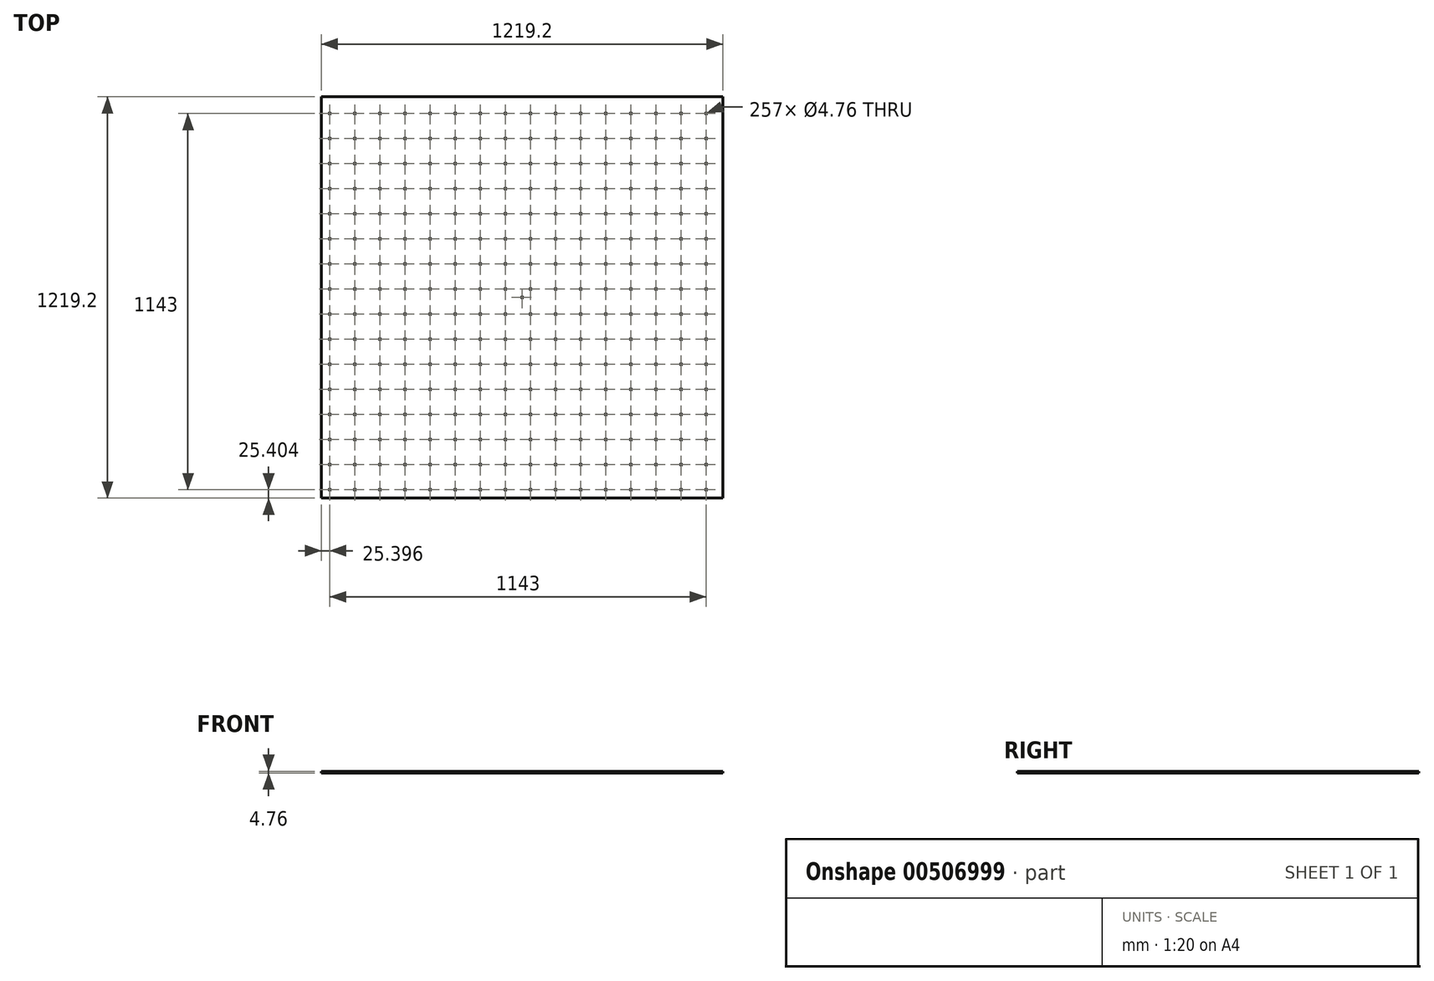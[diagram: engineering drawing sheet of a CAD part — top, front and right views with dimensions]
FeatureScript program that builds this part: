
annotation { "Feature Type Name" : "Feature", "Feature Type Description" : "" }
export const myFeature = defineFeature(function(context is Context, id is Id, definition is map)
    precondition{}
    {
        {
            var Q0;
            Q0=qCreatedBy(makeId("Top.planeOp"),FACE);
            var sketch = newSketch(context, id + "F0", { "sketchPlane" : qUnion([Q0])});
            skLineSegment(sketch, "E0.bottom", {"start": v(-1348, 608.9) * mm, "end": v(-128.8, 608.9) * mm});
            skLineSegment(sketch, "E0.top", {"start": v(-1348, -610.3) * mm, "end": v(-128.8, -610.3) * mm});
            skLineSegment(sketch, "E0.left", {"start": v(-1348, 608.9) * mm, "end": v(-1348, -610.3) * mm});
            skLineSegment(sketch, "E0.right", {"start": v(-128.8, 608.9) * mm, "end": v(-128.8, -610.3) * mm});
            skPoint(sketch, "E0.middle", {"position": v(-738.4, -0.7) * mm});
            skCircle(sketch, "E1", {"center": v(-738.4, -0.7) * mm, "radius": 2.38 * mm});
            skLineSegment(sketch, "E2.bottom", {"start": v(-1348, -610.3) * mm, "end": v(-1322.6, -610.3) * mm, "construction": true});
            skLineSegment(sketch, "E2.top", {"start": v(-1348, -584.9) * mm, "end": v(-1322.6, -584.9) * mm, "construction": true});
            skLineSegment(sketch, "E2.left", {"start": v(-1348, -610.3) * mm, "end": v(-1348, -584.9) * mm, "construction": true});
            skLineSegment(sketch, "E2.right", {"start": v(-1322.6, -610.3) * mm, "end": v(-1322.6, -584.9) * mm, "construction": true});
            skCircle(sketch, "E3", {"center": v(-1322.6, -584.9) * mm, "radius": 2.38 * mm});
            skCircle(sketch, "E4.0.1.0", {"center": v(-1322.6, -508.7) * mm, "radius": 2.38 * mm});
            skCircle(sketch, "E4.0.2.0", {"center": v(-1322.6, -432.5) * mm, "radius": 2.38 * mm});
            skCircle(sketch, "E4.0.3.0", {"center": v(-1322.6, -356.3) * mm, "radius": 2.38 * mm});
            skCircle(sketch, "E4.0.4.0", {"center": v(-1322.6, -280.1) * mm, "radius": 2.38 * mm});
            skCircle(sketch, "E4.0.5.0", {"center": v(-1322.6, -203.9) * mm, "radius": 2.38 * mm});
            skCircle(sketch, "E4.0.6.0", {"center": v(-1322.6, -127.7) * mm, "radius": 2.38 * mm});
            skCircle(sketch, "E4.0.7.0", {"center": v(-1322.6, -51.5) * mm, "radius": 2.38 * mm});
            skCircle(sketch, "E4.0.8.0", {"center": v(-1322.6, 24.7) * mm, "radius": 2.38 * mm});
            skCircle(sketch, "E4.0.9.0", {"center": v(-1322.6, 100.9) * mm, "radius": 2.38 * mm});
            skCircle(sketch, "E4.0.10.0", {"center": v(-1322.6, 177.1) * mm, "radius": 2.38 * mm});
            skCircle(sketch, "E4.1.0.0", {"center": v(-1246.4, -584.9) * mm, "radius": 2.38 * mm});
            skCircle(sketch, "E4.1.1.0", {"center": v(-1246.4, -508.7) * mm, "radius": 2.38 * mm});
            skCircle(sketch, "E4.1.2.0", {"center": v(-1246.4, -432.5) * mm, "radius": 2.38 * mm});
            skCircle(sketch, "E4.1.3.0", {"center": v(-1246.4, -356.3) * mm, "radius": 2.38 * mm});
            skCircle(sketch, "E4.1.4.0", {"center": v(-1246.4, -280.1) * mm, "radius": 2.38 * mm});
            skCircle(sketch, "E4.1.5.0", {"center": v(-1246.4, -203.9) * mm, "radius": 2.38 * mm});
            skCircle(sketch, "E4.1.6.0", {"center": v(-1246.4, -127.7) * mm, "radius": 2.38 * mm});
            skCircle(sketch, "E4.1.7.0", {"center": v(-1246.4, -51.5) * mm, "radius": 2.38 * mm});
            skCircle(sketch, "E4.1.8.0", {"center": v(-1246.4, 24.7) * mm, "radius": 2.38 * mm});
            skCircle(sketch, "E4.1.9.0", {"center": v(-1246.4, 100.9) * mm, "radius": 2.38 * mm});
            skCircle(sketch, "E4.1.10.0", {"center": v(-1246.4, 177.1) * mm, "radius": 2.38 * mm});
            skCircle(sketch, "E4.2.0.0", {"center": v(-1170.2, -584.9) * mm, "radius": 2.38 * mm});
            skCircle(sketch, "E4.2.1.0", {"center": v(-1170.2, -508.7) * mm, "radius": 2.38 * mm});
            skCircle(sketch, "E4.2.2.0", {"center": v(-1170.2, -432.5) * mm, "radius": 2.38 * mm});
            skCircle(sketch, "E4.2.3.0", {"center": v(-1170.2, -356.3) * mm, "radius": 2.38 * mm});
            skCircle(sketch, "E4.2.4.0", {"center": v(-1170.2, -280.1) * mm, "radius": 2.38 * mm});
            skCircle(sketch, "E4.2.5.0", {"center": v(-1170.2, -203.9) * mm, "radius": 2.38 * mm});
            skCircle(sketch, "E4.2.6.0", {"center": v(-1170.2, -127.7) * mm, "radius": 2.38 * mm});
            skCircle(sketch, "E4.2.7.0", {"center": v(-1170.2, -51.5) * mm, "radius": 2.38 * mm});
            skCircle(sketch, "E4.2.8.0", {"center": v(-1170.2, 24.7) * mm, "radius": 2.38 * mm});
            skCircle(sketch, "E4.2.9.0", {"center": v(-1170.2, 100.9) * mm, "radius": 2.38 * mm});
            skCircle(sketch, "E4.2.10.0", {"center": v(-1170.2, 177.1) * mm, "radius": 2.38 * mm});
            skCircle(sketch, "E4.3.0.0", {"center": v(-1094, -584.9) * mm, "radius": 2.38 * mm});
            skCircle(sketch, "E4.3.1.0", {"center": v(-1094, -508.7) * mm, "radius": 2.38 * mm});
            skCircle(sketch, "E4.3.2.0", {"center": v(-1094, -432.5) * mm, "radius": 2.38 * mm});
            skCircle(sketch, "E4.3.3.0", {"center": v(-1094, -356.3) * mm, "radius": 2.38 * mm});
            skCircle(sketch, "E4.3.4.0", {"center": v(-1094, -280.1) * mm, "radius": 2.38 * mm});
            skCircle(sketch, "E4.3.5.0", {"center": v(-1094, -203.9) * mm, "radius": 2.38 * mm});
            skCircle(sketch, "E4.3.6.0", {"center": v(-1094, -127.7) * mm, "radius": 2.38 * mm});
            skCircle(sketch, "E4.3.7.0", {"center": v(-1094, -51.5) * mm, "radius": 2.38 * mm});
            skCircle(sketch, "E4.3.8.0", {"center": v(-1094, 24.7) * mm, "radius": 2.38 * mm});
            skCircle(sketch, "E4.3.9.0", {"center": v(-1094, 100.9) * mm, "radius": 2.38 * mm});
            skCircle(sketch, "E4.3.10.0", {"center": v(-1094, 177.1) * mm, "radius": 2.38 * mm});
            skCircle(sketch, "E4.4.0.0", {"center": v(-1017.8, -584.9) * mm, "radius": 2.38 * mm});
            skCircle(sketch, "E4.4.1.0", {"center": v(-1017.8, -508.7) * mm, "radius": 2.38 * mm});
            skCircle(sketch, "E4.4.2.0", {"center": v(-1017.8, -432.5) * mm, "radius": 2.38 * mm});
            skCircle(sketch, "E4.4.3.0", {"center": v(-1017.8, -356.3) * mm, "radius": 2.38 * mm});
            skCircle(sketch, "E4.4.4.0", {"center": v(-1017.8, -280.1) * mm, "radius": 2.38 * mm});
            skCircle(sketch, "E4.4.5.0", {"center": v(-1017.8, -203.9) * mm, "radius": 2.38 * mm});
            skCircle(sketch, "E4.4.6.0", {"center": v(-1017.8, -127.7) * mm, "radius": 2.38 * mm});
            skCircle(sketch, "E4.4.7.0", {"center": v(-1017.8, -51.5) * mm, "radius": 2.38 * mm});
            skCircle(sketch, "E4.4.8.0", {"center": v(-1017.8, 24.7) * mm, "radius": 2.38 * mm});
            skCircle(sketch, "E4.4.9.0", {"center": v(-1017.8, 100.9) * mm, "radius": 2.38 * mm});
            skCircle(sketch, "E4.4.10.0", {"center": v(-1017.8, 177.1) * mm, "radius": 2.38 * mm});
            skCircle(sketch, "E4.5.0.0", {"center": v(-941.6, -584.9) * mm, "radius": 2.38 * mm});
            skCircle(sketch, "E4.5.1.0", {"center": v(-941.6, -508.7) * mm, "radius": 2.38 * mm});
            skCircle(sketch, "E4.5.2.0", {"center": v(-941.6, -432.5) * mm, "radius": 2.38 * mm});
            skCircle(sketch, "E4.5.3.0", {"center": v(-941.6, -356.3) * mm, "radius": 2.38 * mm});
            skCircle(sketch, "E4.5.4.0", {"center": v(-941.6, -280.1) * mm, "radius": 2.38 * mm});
            skCircle(sketch, "E4.5.5.0", {"center": v(-941.6, -203.9) * mm, "radius": 2.38 * mm});
            skCircle(sketch, "E4.5.6.0", {"center": v(-941.6, -127.7) * mm, "radius": 2.38 * mm});
            skCircle(sketch, "E4.5.7.0", {"center": v(-941.6, -51.5) * mm, "radius": 2.38 * mm});
            skCircle(sketch, "E4.5.8.0", {"center": v(-941.6, 24.7) * mm, "radius": 2.38 * mm});
            skCircle(sketch, "E4.5.9.0", {"center": v(-941.6, 100.9) * mm, "radius": 2.38 * mm});
            skCircle(sketch, "E4.5.10.0", {"center": v(-941.6, 177.1) * mm, "radius": 2.38 * mm});
            skCircle(sketch, "E4.6.0.0", {"center": v(-865.4, -584.9) * mm, "radius": 2.38 * mm});
            skCircle(sketch, "E4.6.1.0", {"center": v(-865.4, -508.7) * mm, "radius": 2.38 * mm});
            skCircle(sketch, "E4.6.2.0", {"center": v(-865.4, -432.5) * mm, "radius": 2.38 * mm});
            skCircle(sketch, "E4.6.3.0", {"center": v(-865.4, -356.3) * mm, "radius": 2.38 * mm});
            skCircle(sketch, "E4.6.4.0", {"center": v(-865.4, -280.1) * mm, "radius": 2.38 * mm});
            skCircle(sketch, "E4.6.5.0", {"center": v(-865.4, -203.9) * mm, "radius": 2.38 * mm});
            skCircle(sketch, "E4.6.6.0", {"center": v(-865.4, -127.7) * mm, "radius": 2.38 * mm});
            skCircle(sketch, "E4.6.7.0", {"center": v(-865.4, -51.5) * mm, "radius": 2.38 * mm});
            skCircle(sketch, "E4.6.8.0", {"center": v(-865.4, 24.7) * mm, "radius": 2.38 * mm});
            skCircle(sketch, "E4.6.9.0", {"center": v(-865.4, 100.9) * mm, "radius": 2.38 * mm});
            skCircle(sketch, "E4.6.10.0", {"center": v(-865.4, 177.1) * mm, "radius": 2.38 * mm});
            skCircle(sketch, "E4.7.0.0", {"center": v(-789.2, -584.9) * mm, "radius": 2.38 * mm});
            skCircle(sketch, "E4.7.1.0", {"center": v(-789.2, -508.7) * mm, "radius": 2.38 * mm});
            skCircle(sketch, "E4.7.2.0", {"center": v(-789.2, -432.5) * mm, "radius": 2.38 * mm});
            skCircle(sketch, "E4.7.3.0", {"center": v(-789.2, -356.3) * mm, "radius": 2.38 * mm});
            skCircle(sketch, "E4.7.4.0", {"center": v(-789.2, -280.1) * mm, "radius": 2.38 * mm});
            skCircle(sketch, "E4.7.5.0", {"center": v(-789.2, -203.9) * mm, "radius": 2.38 * mm});
            skCircle(sketch, "E4.7.6.0", {"center": v(-789.2, -127.7) * mm, "radius": 2.38 * mm});
            skCircle(sketch, "E4.7.7.0", {"center": v(-789.2, -51.5) * mm, "radius": 2.38 * mm});
            skCircle(sketch, "E4.7.8.0", {"center": v(-789.2, 24.7) * mm, "radius": 2.38 * mm});
            skCircle(sketch, "E4.7.9.0", {"center": v(-789.2, 100.9) * mm, "radius": 2.38 * mm});
            skCircle(sketch, "E4.7.10.0", {"center": v(-789.2, 177.1) * mm, "radius": 2.38 * mm});
            skCircle(sketch, "E4.8.0.0", {"center": v(-713, -584.9) * mm, "radius": 2.38 * mm});
            skCircle(sketch, "E4.8.1.0", {"center": v(-713, -508.7) * mm, "radius": 2.38 * mm});
            skCircle(sketch, "E4.8.2.0", {"center": v(-713, -432.5) * mm, "radius": 2.38 * mm});
            skCircle(sketch, "E4.8.3.0", {"center": v(-713, -356.3) * mm, "radius": 2.38 * mm});
            skCircle(sketch, "E4.8.4.0", {"center": v(-713, -280.1) * mm, "radius": 2.38 * mm});
            skCircle(sketch, "E4.8.5.0", {"center": v(-713, -203.9) * mm, "radius": 2.38 * mm});
            skCircle(sketch, "E4.8.6.0", {"center": v(-713, -127.7) * mm, "radius": 2.38 * mm});
            skCircle(sketch, "E4.8.7.0", {"center": v(-713, -51.5) * mm, "radius": 2.38 * mm});
            skCircle(sketch, "E4.8.8.0", {"center": v(-713, 24.7) * mm, "radius": 2.38 * mm});
            skCircle(sketch, "E4.8.9.0", {"center": v(-713, 100.9) * mm, "radius": 2.38 * mm});
            skCircle(sketch, "E4.8.10.0", {"center": v(-713, 177.1) * mm, "radius": 2.38 * mm});
            skCircle(sketch, "E4.9.0.0", {"center": v(-636.8, -584.9) * mm, "radius": 2.38 * mm});
            skCircle(sketch, "E4.9.1.0", {"center": v(-636.8, -508.7) * mm, "radius": 2.38 * mm});
            skCircle(sketch, "E4.9.2.0", {"center": v(-636.8, -432.5) * mm, "radius": 2.38 * mm});
            skCircle(sketch, "E4.9.3.0", {"center": v(-636.8, -356.3) * mm, "radius": 2.38 * mm});
            skCircle(sketch, "E4.9.4.0", {"center": v(-636.8, -280.1) * mm, "radius": 2.38 * mm});
            skCircle(sketch, "E4.9.5.0", {"center": v(-636.8, -203.9) * mm, "radius": 2.38 * mm});
            skCircle(sketch, "E4.9.6.0", {"center": v(-636.8, -127.7) * mm, "radius": 2.38 * mm});
            skCircle(sketch, "E4.9.7.0", {"center": v(-636.8, -51.5) * mm, "radius": 2.38 * mm});
            skCircle(sketch, "E4.9.8.0", {"center": v(-636.8, 24.7) * mm, "radius": 2.38 * mm});
            skCircle(sketch, "E4.9.9.0", {"center": v(-636.8, 100.9) * mm, "radius": 2.38 * mm});
            skCircle(sketch, "E4.9.10.0", {"center": v(-636.8, 177.1) * mm, "radius": 2.38 * mm});
            skCircle(sketch, "E4.10.0.0", {"center": v(-560.6, -584.9) * mm, "radius": 2.38 * mm});
            skCircle(sketch, "E4.10.1.0", {"center": v(-560.6, -508.7) * mm, "radius": 2.38 * mm});
            skCircle(sketch, "E4.10.2.0", {"center": v(-560.6, -432.5) * mm, "radius": 2.38 * mm});
            skCircle(sketch, "E4.10.3.0", {"center": v(-560.6, -356.3) * mm, "radius": 2.38 * mm});
            skCircle(sketch, "E4.10.4.0", {"center": v(-560.6, -280.1) * mm, "radius": 2.38 * mm});
            skCircle(sketch, "E4.10.5.0", {"center": v(-560.6, -203.9) * mm, "radius": 2.38 * mm});
            skCircle(sketch, "E4.10.6.0", {"center": v(-560.6, -127.7) * mm, "radius": 2.38 * mm});
            skCircle(sketch, "E4.10.7.0", {"center": v(-560.6, -51.5) * mm, "radius": 2.38 * mm});
            skCircle(sketch, "E4.10.8.0", {"center": v(-560.6, 24.7) * mm, "radius": 2.38 * mm});
            skCircle(sketch, "E4.10.9.0", {"center": v(-560.6, 100.9) * mm, "radius": 2.38 * mm});
            skCircle(sketch, "E4.10.10.0", {"center": v(-560.6, 177.1) * mm, "radius": 2.38 * mm});
            skCircle(sketch, "E4.11.0.0", {"center": v(-484.4, -584.9) * mm, "radius": 2.38 * mm});
            skCircle(sketch, "E4.11.1.0", {"center": v(-484.4, -508.7) * mm, "radius": 2.38 * mm});
            skCircle(sketch, "E4.11.2.0", {"center": v(-484.4, -432.5) * mm, "radius": 2.38 * mm});
            skCircle(sketch, "E4.11.3.0", {"center": v(-484.4, -356.3) * mm, "radius": 2.38 * mm});
            skCircle(sketch, "E4.11.4.0", {"center": v(-484.4, -280.1) * mm, "radius": 2.38 * mm});
            skCircle(sketch, "E4.11.5.0", {"center": v(-484.4, -203.9) * mm, "radius": 2.38 * mm});
            skCircle(sketch, "E4.11.6.0", {"center": v(-484.4, -127.7) * mm, "radius": 2.38 * mm});
            skCircle(sketch, "E4.11.7.0", {"center": v(-484.4, -51.5) * mm, "radius": 2.38 * mm});
            skCircle(sketch, "E4.11.8.0", {"center": v(-484.4, 24.7) * mm, "radius": 2.38 * mm});
            skCircle(sketch, "E4.11.9.0", {"center": v(-484.4, 100.9) * mm, "radius": 2.38 * mm});
            skCircle(sketch, "E4.11.10.0", {"center": v(-484.4, 177.1) * mm, "radius": 2.38 * mm});
            skLineSegment(sketch, "E4.direction1", {"start": v(-1322.6, -584.9) * mm, "end": v(-1246.4, -584.9) * mm, "construction": true});
            skLineSegment(sketch, "E4.direction2", {"start": v(-1322.6, -584.9) * mm, "end": v(-1322.6, -508.7) * mm, "construction": true});
            skCircle(sketch, "E5.0.12.0", {"center": v(-408.2, -584.9) * mm, "radius": 2.38 * mm});
            skCircle(sketch, "E5.0.12.1", {"center": v(-408.2, -508.7) * mm, "radius": 2.38 * mm});
            skCircle(sketch, "E5.0.12.2", {"center": v(-408.2, -432.5) * mm, "radius": 2.38 * mm});
            skCircle(sketch, "E5.0.12.3", {"center": v(-408.2, -356.3) * mm, "radius": 2.38 * mm});
            skCircle(sketch, "E5.0.12.4", {"center": v(-408.2, -280.1) * mm, "radius": 2.38 * mm});
            skCircle(sketch, "E5.0.12.5", {"center": v(-408.2, -203.9) * mm, "radius": 2.38 * mm});
            skCircle(sketch, "E5.0.12.6", {"center": v(-408.2, -127.7) * mm, "radius": 2.38 * mm});
            skCircle(sketch, "E5.0.12.7", {"center": v(-408.2, -51.5) * mm, "radius": 2.38 * mm});
            skCircle(sketch, "E5.0.12.8", {"center": v(-408.2, 24.7) * mm, "radius": 2.38 * mm});
            skCircle(sketch, "E5.0.12.9", {"center": v(-408.2, 100.9) * mm, "radius": 2.38 * mm});
            skCircle(sketch, "E5.0.12.10", {"center": v(-408.2, 177.1) * mm, "radius": 2.38 * mm});
            skCircle(sketch, "E5.0.13.0", {"center": v(-332, -584.9) * mm, "radius": 2.38 * mm});
            skCircle(sketch, "E5.0.13.1", {"center": v(-332, -508.7) * mm, "radius": 2.38 * mm});
            skCircle(sketch, "E5.0.13.2", {"center": v(-332, -432.5) * mm, "radius": 2.38 * mm});
            skCircle(sketch, "E5.0.13.3", {"center": v(-332, -356.3) * mm, "radius": 2.38 * mm});
            skCircle(sketch, "E5.0.13.4", {"center": v(-332, -280.1) * mm, "radius": 2.38 * mm});
            skCircle(sketch, "E5.0.13.5", {"center": v(-332, -203.9) * mm, "radius": 2.38 * mm});
            skCircle(sketch, "E5.0.13.6", {"center": v(-332, -127.7) * mm, "radius": 2.38 * mm});
            skCircle(sketch, "E5.0.13.7", {"center": v(-332, -51.5) * mm, "radius": 2.38 * mm});
            skCircle(sketch, "E5.0.13.8", {"center": v(-332, 24.7) * mm, "radius": 2.38 * mm});
            skCircle(sketch, "E5.0.13.9", {"center": v(-332, 100.9) * mm, "radius": 2.38 * mm});
            skCircle(sketch, "E5.0.13.10", {"center": v(-332, 177.1) * mm, "radius": 2.38 * mm});
            skCircle(sketch, "E5.0.14.0", {"center": v(-255.8, -584.9) * mm, "radius": 2.38 * mm});
            skCircle(sketch, "E5.0.14.1", {"center": v(-255.8, -508.7) * mm, "radius": 2.38 * mm});
            skCircle(sketch, "E5.0.14.2", {"center": v(-255.8, -432.5) * mm, "radius": 2.38 * mm});
            skCircle(sketch, "E5.0.14.3", {"center": v(-255.8, -356.3) * mm, "radius": 2.38 * mm});
            skCircle(sketch, "E5.0.14.4", {"center": v(-255.8, -280.1) * mm, "radius": 2.38 * mm});
            skCircle(sketch, "E5.0.14.5", {"center": v(-255.8, -203.9) * mm, "radius": 2.38 * mm});
            skCircle(sketch, "E5.0.14.6", {"center": v(-255.8, -127.7) * mm, "radius": 2.38 * mm});
            skCircle(sketch, "E5.0.14.7", {"center": v(-255.8, -51.5) * mm, "radius": 2.38 * mm});
            skCircle(sketch, "E5.0.14.8", {"center": v(-255.8, 24.7) * mm, "radius": 2.38 * mm});
            skCircle(sketch, "E5.0.14.9", {"center": v(-255.8, 100.9) * mm, "radius": 2.38 * mm});
            skCircle(sketch, "E5.0.14.10", {"center": v(-255.8, 177.1) * mm, "radius": 2.38 * mm});
            skCircle(sketch, "E5.0.15.0", {"center": v(-179.6, -584.9) * mm, "radius": 2.38 * mm});
            skCircle(sketch, "E5.0.15.1", {"center": v(-179.6, -508.7) * mm, "radius": 2.38 * mm});
            skCircle(sketch, "E5.0.15.2", {"center": v(-179.6, -432.5) * mm, "radius": 2.38 * mm});
            skCircle(sketch, "E5.0.15.3", {"center": v(-179.6, -356.3) * mm, "radius": 2.38 * mm});
            skCircle(sketch, "E5.0.15.4", {"center": v(-179.6, -280.1) * mm, "radius": 2.38 * mm});
            skCircle(sketch, "E5.0.15.5", {"center": v(-179.6, -203.9) * mm, "radius": 2.38 * mm});
            skCircle(sketch, "E5.0.15.6", {"center": v(-179.6, -127.7) * mm, "radius": 2.38 * mm});
            skCircle(sketch, "E5.0.15.7", {"center": v(-179.6, -51.5) * mm, "radius": 2.38 * mm});
            skCircle(sketch, "E5.0.15.8", {"center": v(-179.6, 24.7) * mm, "radius": 2.38 * mm});
            skCircle(sketch, "E5.0.15.9", {"center": v(-179.6, 100.9) * mm, "radius": 2.38 * mm});
            skCircle(sketch, "E5.0.15.10", {"center": v(-179.6, 177.1) * mm, "radius": 2.38 * mm});
            skCircle(sketch, "E6.0.0.11", {"center": v(-1322.6, 253.3) * mm, "radius": 2.38 * mm});
            skCircle(sketch, "E6.0.0.12", {"center": v(-1322.6, 329.5) * mm, "radius": 2.38 * mm});
            skCircle(sketch, "E6.0.0.13", {"center": v(-1322.6, 405.7) * mm, "radius": 2.38 * mm});
            skCircle(sketch, "E6.0.0.14", {"center": v(-1322.6, 481.9) * mm, "radius": 2.38 * mm});
            skCircle(sketch, "E6.0.0.15", {"center": v(-1322.6, 558.1) * mm, "radius": 2.38 * mm});
            skCircle(sketch, "E6.0.1.11", {"center": v(-1246.4, 253.3) * mm, "radius": 2.38 * mm});
            skCircle(sketch, "E6.0.1.12", {"center": v(-1246.4, 329.5) * mm, "radius": 2.38 * mm});
            skCircle(sketch, "E6.0.1.13", {"center": v(-1246.4, 405.7) * mm, "radius": 2.38 * mm});
            skCircle(sketch, "E6.0.1.14", {"center": v(-1246.4, 481.9) * mm, "radius": 2.38 * mm});
            skCircle(sketch, "E6.0.1.15", {"center": v(-1246.4, 558.1) * mm, "radius": 2.38 * mm});
            skCircle(sketch, "E6.0.2.11", {"center": v(-1170.2, 253.3) * mm, "radius": 2.38 * mm});
            skCircle(sketch, "E6.0.2.12", {"center": v(-1170.2, 329.5) * mm, "radius": 2.38 * mm});
            skCircle(sketch, "E6.0.2.13", {"center": v(-1170.2, 405.7) * mm, "radius": 2.38 * mm});
            skCircle(sketch, "E6.0.2.14", {"center": v(-1170.2, 481.9) * mm, "radius": 2.38 * mm});
            skCircle(sketch, "E6.0.2.15", {"center": v(-1170.2, 558.1) * mm, "radius": 2.38 * mm});
            skCircle(sketch, "E6.0.3.11", {"center": v(-1094, 253.3) * mm, "radius": 2.38 * mm});
            skCircle(sketch, "E6.0.3.12", {"center": v(-1094, 329.5) * mm, "radius": 2.38 * mm});
            skCircle(sketch, "E6.0.3.13", {"center": v(-1094, 405.7) * mm, "radius": 2.38 * mm});
            skCircle(sketch, "E6.0.3.14", {"center": v(-1094, 481.9) * mm, "radius": 2.38 * mm});
            skCircle(sketch, "E6.0.3.15", {"center": v(-1094, 558.1) * mm, "radius": 2.38 * mm});
            skCircle(sketch, "E6.0.4.11", {"center": v(-1017.8, 253.3) * mm, "radius": 2.38 * mm});
            skCircle(sketch, "E6.0.4.12", {"center": v(-1017.8, 329.5) * mm, "radius": 2.38 * mm});
            skCircle(sketch, "E6.0.4.13", {"center": v(-1017.8, 405.7) * mm, "radius": 2.38 * mm});
            skCircle(sketch, "E6.0.4.14", {"center": v(-1017.8, 481.9) * mm, "radius": 2.38 * mm});
            skCircle(sketch, "E6.0.4.15", {"center": v(-1017.8, 558.1) * mm, "radius": 2.38 * mm});
            skCircle(sketch, "E6.0.5.11", {"center": v(-941.6, 253.3) * mm, "radius": 2.38 * mm});
            skCircle(sketch, "E6.0.5.12", {"center": v(-941.6, 329.5) * mm, "radius": 2.38 * mm});
            skCircle(sketch, "E6.0.5.13", {"center": v(-941.6, 405.7) * mm, "radius": 2.38 * mm});
            skCircle(sketch, "E6.0.5.14", {"center": v(-941.6, 481.9) * mm, "radius": 2.38 * mm});
            skCircle(sketch, "E6.0.5.15", {"center": v(-941.6, 558.1) * mm, "radius": 2.38 * mm});
            skCircle(sketch, "E6.0.6.11", {"center": v(-865.4, 253.3) * mm, "radius": 2.38 * mm});
            skCircle(sketch, "E6.0.6.12", {"center": v(-865.4, 329.5) * mm, "radius": 2.38 * mm});
            skCircle(sketch, "E6.0.6.13", {"center": v(-865.4, 405.7) * mm, "radius": 2.38 * mm});
            skCircle(sketch, "E6.0.6.14", {"center": v(-865.4, 481.9) * mm, "radius": 2.38 * mm});
            skCircle(sketch, "E6.0.6.15", {"center": v(-865.4, 558.1) * mm, "radius": 2.38 * mm});
            skCircle(sketch, "E6.0.7.11", {"center": v(-789.2, 253.3) * mm, "radius": 2.38 * mm});
            skCircle(sketch, "E6.0.7.12", {"center": v(-789.2, 329.5) * mm, "radius": 2.38 * mm});
            skCircle(sketch, "E6.0.7.13", {"center": v(-789.2, 405.7) * mm, "radius": 2.38 * mm});
            skCircle(sketch, "E6.0.7.14", {"center": v(-789.2, 481.9) * mm, "radius": 2.38 * mm});
            skCircle(sketch, "E6.0.7.15", {"center": v(-789.2, 558.1) * mm, "radius": 2.38 * mm});
            skCircle(sketch, "E6.0.8.11", {"center": v(-713, 253.3) * mm, "radius": 2.38 * mm});
            skCircle(sketch, "E6.0.8.12", {"center": v(-713, 329.5) * mm, "radius": 2.38 * mm});
            skCircle(sketch, "E6.0.8.13", {"center": v(-713, 405.7) * mm, "radius": 2.38 * mm});
            skCircle(sketch, "E6.0.8.14", {"center": v(-713, 481.9) * mm, "radius": 2.38 * mm});
            skCircle(sketch, "E6.0.8.15", {"center": v(-713, 558.1) * mm, "radius": 2.38 * mm});
            skCircle(sketch, "E6.0.9.11", {"center": v(-636.8, 253.3) * mm, "radius": 2.38 * mm});
            skCircle(sketch, "E6.0.9.12", {"center": v(-636.8, 329.5) * mm, "radius": 2.38 * mm});
            skCircle(sketch, "E6.0.9.13", {"center": v(-636.8, 405.7) * mm, "radius": 2.38 * mm});
            skCircle(sketch, "E6.0.9.14", {"center": v(-636.8, 481.9) * mm, "radius": 2.38 * mm});
            skCircle(sketch, "E6.0.9.15", {"center": v(-636.8, 558.1) * mm, "radius": 2.38 * mm});
            skCircle(sketch, "E6.0.10.11", {"center": v(-560.6, 253.3) * mm, "radius": 2.38 * mm});
            skCircle(sketch, "E6.0.10.12", {"center": v(-560.6, 329.5) * mm, "radius": 2.38 * mm});
            skCircle(sketch, "E6.0.10.13", {"center": v(-560.6, 405.7) * mm, "radius": 2.38 * mm});
            skCircle(sketch, "E6.0.10.14", {"center": v(-560.6, 481.9) * mm, "radius": 2.38 * mm});
            skCircle(sketch, "E6.0.10.15", {"center": v(-560.6, 558.1) * mm, "radius": 2.38 * mm});
            skCircle(sketch, "E6.0.11.11", {"center": v(-484.4, 253.3) * mm, "radius": 2.38 * mm});
            skCircle(sketch, "E6.0.11.12", {"center": v(-484.4, 329.5) * mm, "radius": 2.38 * mm});
            skCircle(sketch, "E6.0.11.13", {"center": v(-484.4, 405.7) * mm, "radius": 2.38 * mm});
            skCircle(sketch, "E6.0.11.14", {"center": v(-484.4, 481.9) * mm, "radius": 2.38 * mm});
            skCircle(sketch, "E6.0.11.15", {"center": v(-484.4, 558.1) * mm, "radius": 2.38 * mm});
            skCircle(sketch, "E6.0.12.11", {"center": v(-408.2, 253.3) * mm, "radius": 2.38 * mm});
            skCircle(sketch, "E6.0.12.12", {"center": v(-408.2, 329.5) * mm, "radius": 2.38 * mm});
            skCircle(sketch, "E6.0.12.13", {"center": v(-408.2, 405.7) * mm, "radius": 2.38 * mm});
            skCircle(sketch, "E6.0.12.14", {"center": v(-408.2, 481.9) * mm, "radius": 2.38 * mm});
            skCircle(sketch, "E6.0.12.15", {"center": v(-408.2, 558.1) * mm, "radius": 2.38 * mm});
            skCircle(sketch, "E6.0.13.11", {"center": v(-332, 253.3) * mm, "radius": 2.38 * mm});
            skCircle(sketch, "E6.0.13.12", {"center": v(-332, 329.5) * mm, "radius": 2.38 * mm});
            skCircle(sketch, "E6.0.13.13", {"center": v(-332, 405.7) * mm, "radius": 2.38 * mm});
            skCircle(sketch, "E6.0.13.14", {"center": v(-332, 481.9) * mm, "radius": 2.38 * mm});
            skCircle(sketch, "E6.0.13.15", {"center": v(-332, 558.1) * mm, "radius": 2.38 * mm});
            skCircle(sketch, "E6.0.14.11", {"center": v(-255.8, 253.3) * mm, "radius": 2.38 * mm});
            skCircle(sketch, "E6.0.14.12", {"center": v(-255.8, 329.5) * mm, "radius": 2.38 * mm});
            skCircle(sketch, "E6.0.14.13", {"center": v(-255.8, 405.7) * mm, "radius": 2.38 * mm});
            skCircle(sketch, "E6.0.14.14", {"center": v(-255.8, 481.9) * mm, "radius": 2.38 * mm});
            skCircle(sketch, "E6.0.14.15", {"center": v(-255.8, 558.1) * mm, "radius": 2.38 * mm});
            skCircle(sketch, "E6.0.15.11", {"center": v(-179.6, 253.3) * mm, "radius": 2.38 * mm});
            skCircle(sketch, "E6.0.15.12", {"center": v(-179.6, 329.5) * mm, "radius": 2.38 * mm});
            skCircle(sketch, "E6.0.15.13", {"center": v(-179.6, 405.7) * mm, "radius": 2.38 * mm});
            skCircle(sketch, "E6.0.15.14", {"center": v(-179.6, 481.9) * mm, "radius": 2.38 * mm});
            skCircle(sketch, "E6.0.15.15", {"center": v(-179.6, 558.1) * mm, "radius": 2.38 * mm});
            skSolve(sketch);
        }
        {
            var Q0;
            Q0=makeQuery(id+"F0.imprint","IMPRINT",FACE,{"disambiguationData":[TD([[makeQuery(id+"F0.imprint","IMPRINT",EDGE,{"derivedFrom":sQuery(id+"F0.wireOp",EDGE,"E0.bottom")}),-1.0]])]});
            extrude(context, id + "F1", {"entities" : qUnion([Q0]), "depth" : 4.76 * mm});
        }
    });
